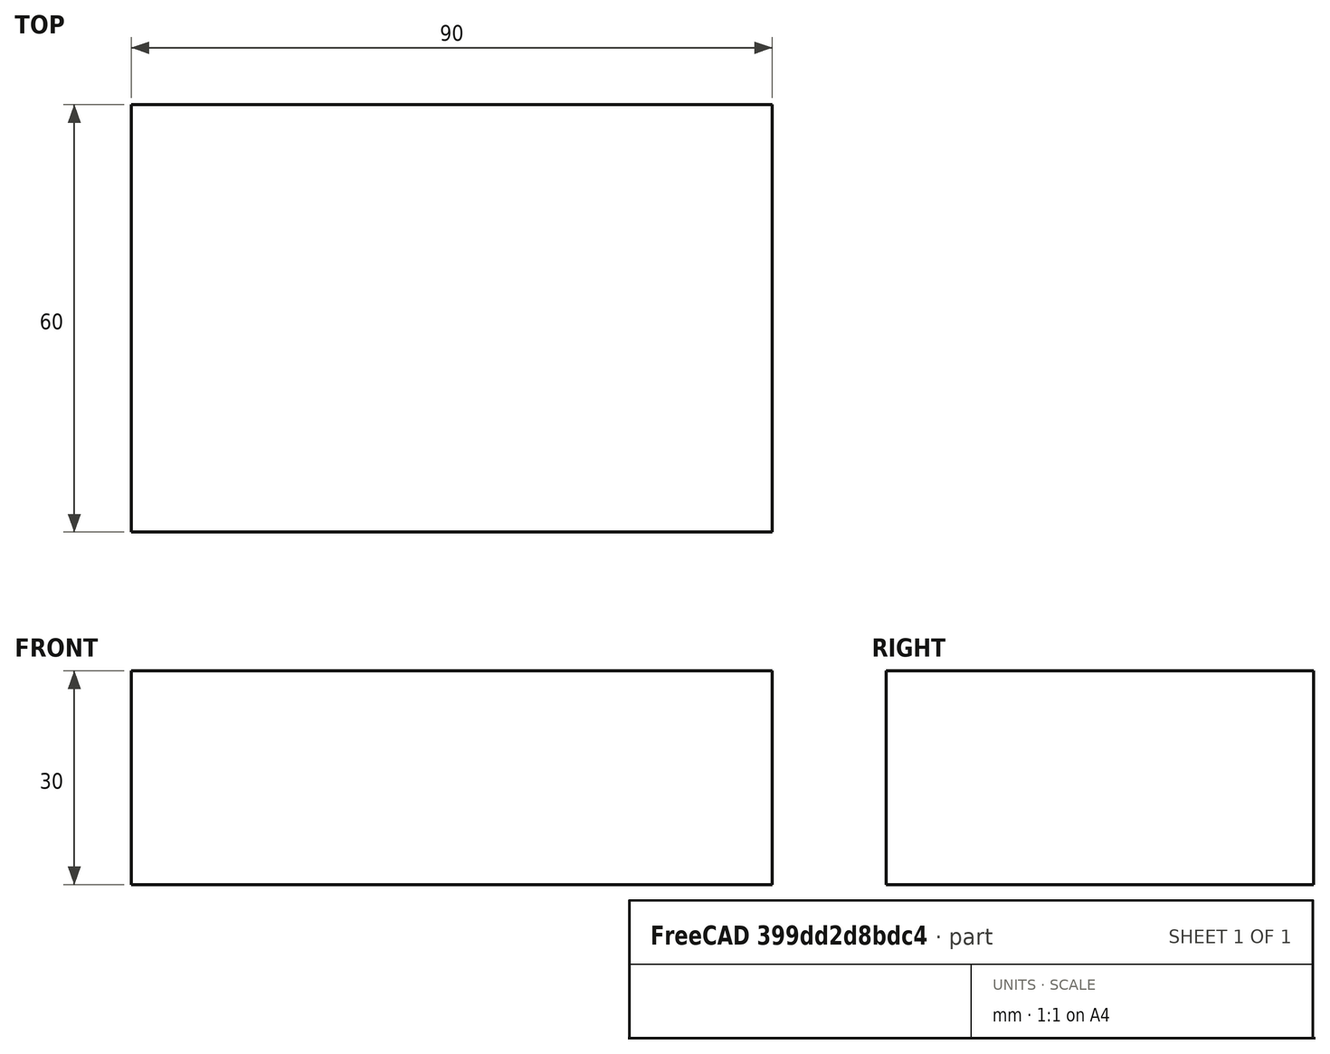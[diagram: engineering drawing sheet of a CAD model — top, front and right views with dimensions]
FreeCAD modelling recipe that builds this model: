
FCSTD DOCUMENT  (FreeCAD 0.21R33771 (Git))
Label: box_90x60x30
License: All rights reserved
LicenseURL: https://en.wikipedia.org/wiki/All_rights_reserved
objects: Sketcher::SketchObject×1, PartDesign::Pad×1, PartDesign::Body×1, App::Part×1, Spreadsheet::Sheet×1
note: 4 computed .brp shape members not serialized (recipe doc carries the construction recipe); baked Part::Feature solids carry a one-line shape summary decoded from their .brp

FEATURE [Sketcher::SketchObject] Sketch
  FullyConstrained = true
  MapMode = 5
  Support = -> [XY_Plane001]
  sketch-geometry (4):
    g0: LineSegment StartX=-45 StartY=-30 StartZ=0 EndX=45 EndY=-30 EndZ=0
    g1: LineSegment StartX=45 StartY=-30 StartZ=0 EndX=45 EndY=30 EndZ=0
    g2: LineSegment StartX=45 StartY=30 StartZ=0 EndX=-45 EndY=30 EndZ=0
    g3: LineSegment StartX=-45 StartY=30 StartZ=0 EndX=-45 EndY=-30 EndZ=0
  constraints (11):
    c: Coincident(g0,g1)
    c: Coincident(g1,g2)
    c: Coincident(g2,g3)
    c: Coincident(g3,g0)
    c: Horizontal(g0)
    c: Horizontal(g2)
    c: Vertical(g1)
    c: Vertical(g3)
    c: DistanceX(g0,g0) = 90
    c: DistanceY(g1,g1) = 60
    c: Symmetric(g1,g0,g-1)
FEATURE [PartDesign::Pad] Pad
  Direction = (0,0,1)
  Length = 30
  Length2 = 10
  Midplane = true
  Profile = -> Sketch
  ReferenceAxis = -> Sketch [N_Axis]
  Type = 0
FEATURE [PartDesign::Body] Body
  Group = -> [Sketch,Pad]
  Origin = -> Origin001
  Tip = -> Pad
FEATURE [App::Part] Part
  Group = -> [Body]
  Origin = -> Origin
FEATURE [Spreadsheet::Sheet] box_90x60x30
  cells = A1='Information of element; A2='________________________; A3='02/09/2024 18:33:18; A4='Document name; B4='Unnamed1; A5='Label of the object; B5='Body; A6='Internal name of the object; B6='Body; A7='Element name; A8='Object Type (Shape); B8='Solid; A9='Object Type; B9='Part::TopoShape; A10='Mouse coordinates; B10='X; C10=0; D10='mm; E10='Y; F10=0; G10='mm; H10='Z; I10=0; J10='mm; A11='Color on selection; A12='Red; B12=0; C12='Green; D12=0; E12='Blue; F12=0; G12='Transparency; H12=0; A13='Object Color (float) ; B13='Red; C13=0.800000011920929; D13='Green; E13=0.800000011920929; F13='Blue; G13=0.800000011920929; H13='Transparency; I13=0; A14='Object Color (int  ) ; B14='Red; C14=204; D14='Green; E14=204; F14='Blue; G14=204; H14='Transparency; I14=0; A15='Object Color (float) ; B15='Red; C15=0.0980392172932625; D15='Green; E15=0.0980392172932625; F15='Blue; G15=0.0980392172932625; H15='Transparency; I15=0; A16='Color Line(s) (int  ) ; B16='Red; C16=25; D16='Green; E16=25; F16='Blue; G16=25; H16='Transparency; I16=0; A17='Color Point(s) (float) ; B17='Red; C17=0.0980392172932625; D17='Green; E17=0.0980392172932625; F17='Blue; G17=0.0980392172932625; H17='Transparency; I17=0; A18='Color Point(s) (int  ) ; B18='Red; C18=25; D18='Green; E18=25; F18='Blue; G18=25; H18='Transparency; I18=0; A19='Length of the object; B19=0; C19='mm; A20='Shape Perimeter; B20=720; C20='mm; A22='Plane; B22=' XY:; C22==0 deg; D22=' coordinates:; E22='[,0.0 , 0.0,]  [,0.0 , 0.0,]; A23='Plane; B23=' YZ:; C23==0 deg; D23=' coordinates:; E23='[,0.0 , 0.0,]  [,0.0 , 0.0,]; A24='Plane; B24=' ZX:; C24==0 deg; D24=' coordinates:; E24='[,0.0 , 0.0,]  [,0.0 , 0.0,]; A25='Shape area; B25=19800; C25='mm2; A26='Face area; B26=0; C26='mm2; A27='Volume of the form; B27=162000; C27='mm3; A28='Mass; B28=1718.82; C28='g; D28=' Density:; E28=10.61; A29='Shape center; B29=' X:; C29=0; D29='mm; E29=' Y:; F29=0; G29='mm; H29=' Z:; I29=0; J29='mm; A30='Center of mass; B30=' X:; C30=0; D30='mm; E30=' Y:; F30=-0; G30='mm; H30=' Z:; I30=0; J30='mm; A31='Overall dimensions; B31=' X:; C31=90; D31='mm; E31=' Y:; F31=60; G31='mm; H31=' Z:; I31=30; J31='mm; A32='Diagonal dimensions; B32=112.2497; C32='mm; A33='Direction; B33=' X:; C33=0; D33=' Y:; E33=0; F33=' Z:; G33=30; A35='Matrix of inertia; B35='mm^5; A36=' X:; B36=60750000; C36=' Y:; D36=0; E36=' Z:; F36=0; G36=' :; H36=0; A37=' X:; B37=0; C37=' Y:; D37=121500000; E37=' Z:; F37=0; G37=' :; H37=0; A38=' X:; B38=0; C38=' Y:; D38=0; E38=' Z:; F38=157950000; G38=' :; H38=0; A39=' X:; B39=0; C39=' Y:; D39=0; E39=' Z:; F39=0; G39=' :; H39=1; A40='Matrix inertia massique; B40='gmm2; A41=' X:; B41=644557.5; +280 more cells
